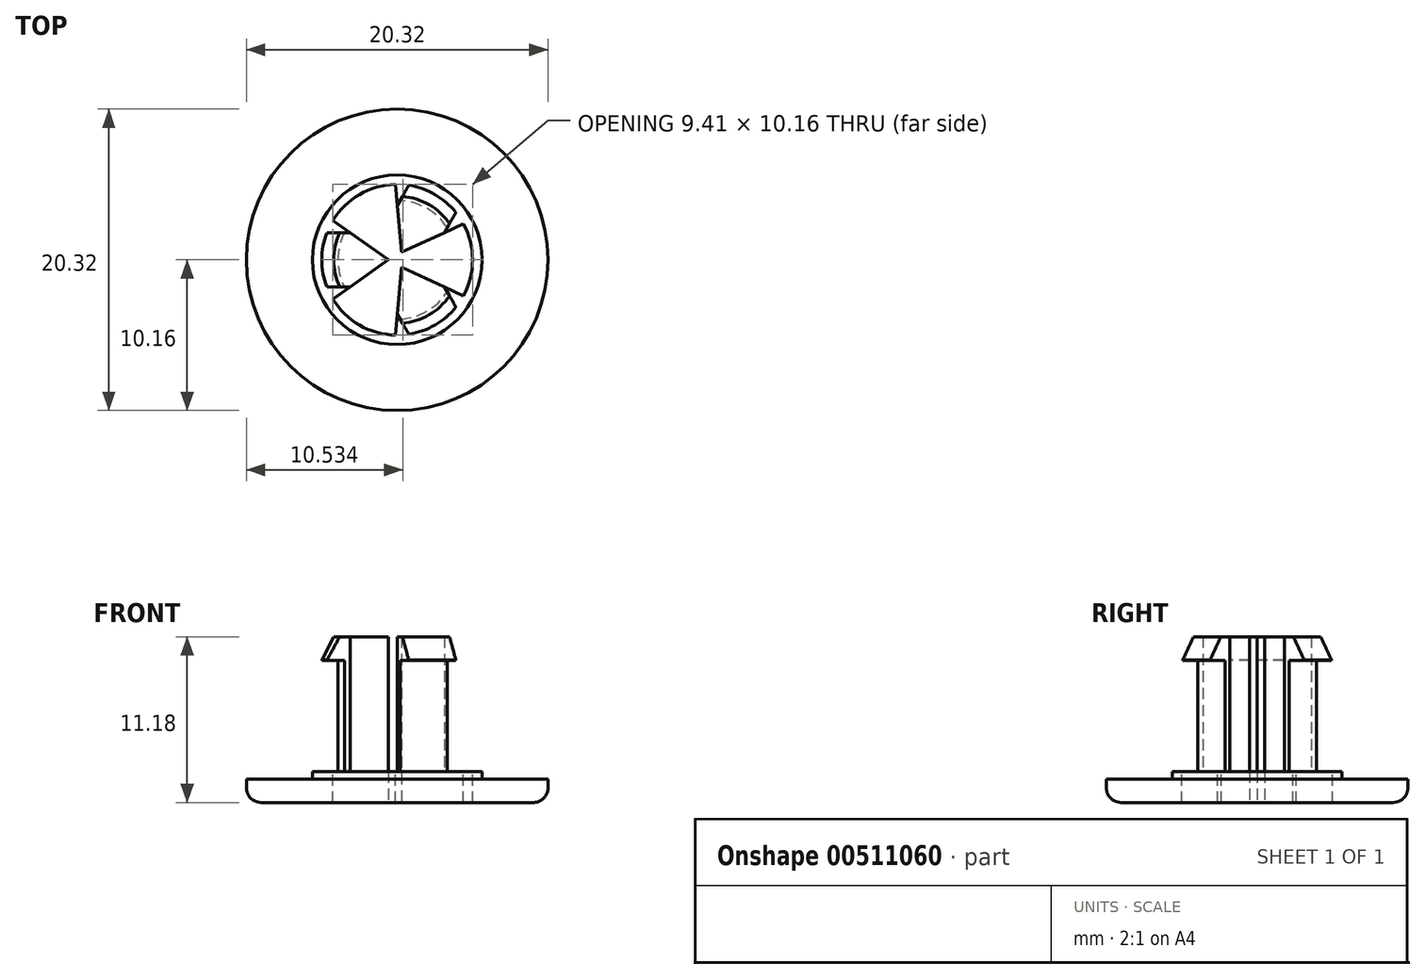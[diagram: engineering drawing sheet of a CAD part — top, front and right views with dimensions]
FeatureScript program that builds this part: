
annotation { "Feature Type Name" : "Feature", "Feature Type Description" : "" }
export const myFeature = defineFeature(function(context is Context, id is Id, definition is map)
    precondition{}
    {
        {
            var Q0;
            Q0=qCreatedBy(makeId("Top.planeOp"),FACE);
            var sketch = newSketch(context, id + "F0", { "sketchPlane" : qUnion([Q0])});
            skCircle(sketch, "E0", {"center": v(0, 0) * mm, "radius": 10.16 * mm});
            skSolve(sketch);
        }
        {
            var Q0;
            Q0=makeQuery(id+"F0.imprint","IMPRINT",FACE,{"disambiguationData":[TD([[makeQuery(id+"F0.imprint","IMPRINT",EDGE,{"derivedFrom":sQuery(id+"F0.wireOp",EDGE,"E0")}),1.0]])]});
            extrude(context, id + "F1", {"entities" : qUnion([Q0]), "depth" : 1.59 * mm});
        }
        {
            var Q0;
            Q0=makeQuery(id+"F1.opExtrude","CAP_FACE",FACE,{"disambiguationData":[OSD([sQuery(id+"F0.wireOp",EDGE,"E0")])],"isStart":false});
            var sketch = newSketch(context, id + "F2", { "sketchPlane" : qUnion([Q0])});
            skCircle(sketch, "E1", {"center": v(0, 0) * mm, "radius": 4 * mm});
            skCircle(sketch, "E2.cCircle", {"center": v(0, 0) * mm, "radius": 3.18 * mm, "construction": true});
            skLineSegment(sketch, "E2.0", {"start": v(3.18, 1.83) * mm, "end": v(3.18, -1.83) * mm});
            skLineSegment(sketch, "E2.1", {"start": v(3.17, -1.83) * mm, "end": v(0, -3.67) * mm});
            skLineSegment(sketch, "E2.2", {"start": v(0, -3.67) * mm, "end": v(-3.18, -1.83) * mm});
            skLineSegment(sketch, "E2.3", {"start": v(-3.18, -1.83) * mm, "end": v(-3.18, 1.83) * mm});
            skLineSegment(sketch, "E2.4", {"start": v(-3.18, 1.83) * mm, "end": v(0, 3.67) * mm});
            skLineSegment(sketch, "E2.5", {"start": v(0, 3.67) * mm, "end": v(3.18, 1.83) * mm});
            skPoint(sketch, "E2.0.midPoint", {"position": v(3.18, 0) * mm});
            skLineSegment(sketch, "E3", {"start": v(0, 3.67) * mm, "end": v(0.3, 0.5) * mm});
            skLineSegment(sketch, "E4", {"start": v(0.3, 0.5) * mm, "end": v(3.17, 1.83) * mm});
            skLineSegment(sketch, "E5", {"start": v(0.3, -0.5) * mm, "end": v(0, -3.67) * mm});
            skLineSegment(sketch, "E6", {"start": v(-0.58, 0) * mm, "end": v(-3.18, -1.83) * mm});
            skLineSegment(sketch, "E7", {"start": v(-3.18, 1.83) * mm, "end": v(-0.58, 0) * mm});
            skLineSegment(sketch, "E8", {"start": v(0.3, -0.5) * mm, "end": v(3.18, -1.83) * mm});
            skSolve(sketch);
        }
        {
            var Q0;
            Q0=makeQuery(id+"F2.imprint","IMPRINT",FACE,{"disambiguationData":[TD([[makeQuery(id+"F2.imprint","IMPRINT",EDGE,{"derivedFrom":sQuery(id+"F2.wireOp",EDGE,"E1")}),1.0]])]});
            var Q1;
            Q1=makeQuery(id+"F2.imprint","IMPRINT",FACE,{"disambiguationData":[TD([[makeQuery(id+"F2.imprint","IMPRINT",EDGE,{"derivedFrom":sQuery(id+"F2.wireOp",EDGE,"E2.3")}),-1.0]])]});
            var Q2;
            Q2=makeQuery(id+"F2.imprint","IMPRINT",FACE,{"disambiguationData":[TD([[makeQuery(id+"F2.imprint","IMPRINT",EDGE,{"derivedFrom":sQuery(id+"F2.wireOp",EDGE,"E2.5")}),-1.0]])]});
            var Q3;
            Q3=makeQuery(id+"F2.imprint","IMPRINT",FACE,{"disambiguationData":[TD([[makeQuery(id+"F2.imprint","IMPRINT",EDGE,{"derivedFrom":sQuery(id+"F2.wireOp",EDGE,"E2.1")}),-1.0]])]});
            extrude(context, id + "F3", {"entities" : qUnion([Q0, Q1, Q2, Q3]), "operationType" : NewBodyOperationType.ADD, "depth" : 8 * mm, "offsetDistance" : 25.4 * mm});
        }
        {
            var Q0;
            Q0=makeQuery(id+"F3.opExtrude","CAP_FACE",FACE,{"disambiguationData":[OSD([sQuery(id+"F2.wireOp",EDGE,"E1"),sQuery(id+"F2.wireOp",EDGE,"E2.0"),sQuery(id+"F2.wireOp",EDGE,"E2.2"),sQuery(id+"F2.wireOp",EDGE,"E2.4"),sQuery(id+"F2.wireOp",EDGE,"E3"),sQuery(id+"F2.wireOp",EDGE,"E4"),sQuery(id+"F2.wireOp",EDGE,"E5"),sQuery(id+"F2.wireOp",EDGE,"E6"),sQuery(id+"F2.wireOp",EDGE,"E7"),sQuery(id+"F2.wireOp",EDGE,"E8")])],"isStart":false});
            var sketch = newSketch(context, id + "F4", { "sketchPlane" : qUnion([Q0])});
            skLineSegment(sketch, "E9", {"start": v(0, 3.67) * mm, "end": v(3.18, 1.83) * mm});
            skLineSegment(sketch, "E10", {"start": v(3.17, 1.83) * mm, "end": v(3.37, 2.16) * mm});
            skLineSegment(sketch, "E11", {"start": v(0, 3.67) * mm, "end": v(0.2, 4) * mm});
            skLineSegment(sketch, "E12", {"start": v(-3.18, 1.83) * mm, "end": v(-3.18, -1.83) * mm});
            skLineSegment(sketch, "E13", {"start": v(-3.18, -1.83) * mm, "end": v(-3.56, -1.83) * mm});
            skLineSegment(sketch, "E14", {"start": v(-3.18, 1.83) * mm, "end": v(-3.56, 1.83) * mm});
            skLineSegment(sketch, "E15", {"start": v(0, -3.67) * mm, "end": v(3.18, -1.83) * mm});
            skLineSegment(sketch, "E16", {"start": v(3.18, -1.83) * mm, "end": v(3.37, -2.16) * mm});
            skLineSegment(sketch, "E17", {"start": v(0, -3.67) * mm, "end": v(0.2, -4) * mm});
            skSolve(sketch);
        }
        {
            var Q0;
            {var subQ0=sQuery(id+"F4.wireOp",EDGE,"E11");Q0=makeQuery(id+"F4.imprint","IMPRINT",FACE,{"disambiguationData":[TD([[makeQuery(id+"F4.imprint","IMPRINT",EDGE,{"derivedFrom":subQ0}),1.0]])]});}
            var Q1;
            {var subQ0=sQuery(id+"F4.wireOp",EDGE,"E10");Q1=makeQuery(id+"F4.imprint","IMPRINT",FACE,{"disambiguationData":[TD([[makeQuery(id+"F4.imprint","IMPRINT",EDGE,{"derivedFrom":subQ0}),-1.0]])]});}
            var Q2;
            {var subQ0=sQuery(id+"F4.wireOp",EDGE,"E13");Q2=makeQuery(id+"F4.imprint","IMPRINT",FACE,{"disambiguationData":[TD([[makeQuery(id+"F4.imprint","IMPRINT",EDGE,{"derivedFrom":subQ0}),1.0]])]});}
            var Q3;
            {var subQ0=sQuery(id+"F0.wireOp",EDGE,"E0");Q3=makeQuery(id+"F3.boolean.opBoolean","SPLIT",FACE,{"disambiguationData":[TD([makeQuery(id+"F1.opExtrude","SWEPT_FACE",FACE,{"disambiguationData":[OSD([subQ0])]})])],"derivedFrom":makeQuery(id+"F1.opExtrude","CAP_FACE",FACE,{"disambiguationData":[OSD([subQ0])],"isStart":false})});}
            extrude(context, id + "F5", {"entities" : qUnion([Q0, Q1, Q2]), "operationType" : NewBodyOperationType.REMOVE, "endBound" : BoundingType.UP_TO_SURFACE, "oppositeDirection" : true, "depth" : 25.4 * mm, "endBoundEntityFace" : qUnion([Q3]), "offsetDistance" : 25.4 * mm});
        }
        {
            var Q0;
            {var subQ0=sQuery(id+"F2.wireOp",EDGE,"E2.2");var subQ1=sQuery(id+"F2.wireOp",EDGE,"E1");var subQ2=sQuery(id+"F2.wireOp",EDGE,"E2.4");var subQ3=sQuery(id+"F2.wireOp",EDGE,"E2.0");var subQ4=sQuery(id+"F0.wireOp",EDGE,"E0");var subQ5=makeQuery(id+"F1.opExtrude","CAP_FACE",FACE,{"disambiguationData":[OSD([subQ4])],"isStart":false});Q0=makeQuery(id+"F5.boolean.opBoolean","MERGE",FACE,{"derivedFrom":[makeQuery(id+"F3.boolean.opBoolean","SPLIT",FACE,{"disambiguationData":[TD([makeQuery(id+"F1.opExtrude","SWEPT_FACE",FACE,{"disambiguationData":[OSD([subQ4])]})])],"derivedFrom":subQ5}),makeQuery(id+"F3.boolean.opBoolean","SPLIT",FACE,{"disambiguationData":[TD([makeQuery(id+"F3.opExtrude","SWEPT_FACE",FACE,{"disambiguationData":[OSD([subQ3])]})])],"derivedFrom":subQ5}),makeQuery(id+"F5.opExtrude","CAP_FACE",FACE,{"disambiguationData":[OSD([subQ1,subQ3,sQuery(id+"F4.wireOp",EDGE,"E10"),sQuery(id+"F4.wireOp",EDGE,"E16")])],"isStart":false}),makeQuery(id+"F5.opExtrude","CAP_FACE",FACE,{"disambiguationData":[OSD([subQ1,subQ2,sQuery(id+"F4.wireOp",EDGE,"E11"),sQuery(id+"F4.wireOp",EDGE,"E14")])],"isStart":false}),makeQuery(id+"F5.opExtrude","CAP_FACE",FACE,{"disambiguationData":[OSD([subQ1,subQ0,sQuery(id+"F4.wireOp",EDGE,"E13"),sQuery(id+"F4.wireOp",EDGE,"E17")])],"isStart":false})]});}
            var sketch = newSketch(context, id + "F6", { "sketchPlane" : qUnion([Q0])});
            skCircle(sketch, "E18", {"center": v(0, 0) * mm, "radius": 5.71 * mm});
            skSolve(sketch);
        }
        {
            var Q0;
            Q0 = qSketchRegion(id + "F6", true);
            extrude(context, id + "F7", {"entities" : qUnion([Q0]), "operationType" : NewBodyOperationType.ADD, "depth" : .5 * mm, "offsetDistance" : 25.4 * mm});
        }
        {
            var Q0;
            {var subQ0=sQuery(id+"F2.wireOp",EDGE,"E4");var subQ1=sQuery(id+"F2.wireOp",EDGE,"E3");var subQ2=sQuery(id+"F2.wireOp",EDGE,"E1");Q0=makeQuery(id+"F5.boolean.opBoolean","SPLIT",FACE,{"disambiguationData":[TD([makeQuery(id+"F3.opExtrude","SWEPT_FACE",FACE,{"disambiguationData":[OSD([subQ1])]})])],"derivedFrom":makeQuery(id+"F3.opExtrude","CAP_FACE",FACE,{"disambiguationData":[OSD([subQ2,sQuery(id+"F2.wireOp",EDGE,"E2.0"),sQuery(id+"F2.wireOp",EDGE,"E2.2"),sQuery(id+"F2.wireOp",EDGE,"E2.4"),subQ1,subQ0,sQuery(id+"F2.wireOp",EDGE,"E5"),sQuery(id+"F2.wireOp",EDGE,"E6"),sQuery(id+"F2.wireOp",EDGE,"E7"),sQuery(id+"F2.wireOp",EDGE,"E8")])],"isStart":false})});}
            var sketch = newSketch(context, id + "F8", { "sketchPlane" : qUnion([Q0])});
            skLineSegment(sketch, "E19.0", {"start": v(0, 3.67) * mm, "end": v(0.3, 0.5) * mm});
            skLineSegment(sketch, "E20.0", {"start": v(0, 3.67) * mm, "end": v(0.2, 4) * mm});
            skArc(sketch, "E21.0", {"start": v(3.37, 2.16) * mm, "mid": v(2, 3.46) * mm, "end": v(0.2, 4) * mm});
            skLineSegment(sketch, "E22.0", {"start": v(3.18, 1.83) * mm, "end": v(3.37, 2.16) * mm});
            skLineSegment(sketch, "E23.0", {"start": v(0.3, 0.5) * mm, "end": v(3.18, 1.83) * mm});
            skLineSegment(sketch, "E24.0", {"start": v(0.3, -0.5) * mm, "end": v(3.17, -1.83) * mm});
            skLineSegment(sketch, "E25.0", {"start": v(0.3, -0.5) * mm, "end": v(0, -3.67) * mm});
            skLineSegment(sketch, "E26.0", {"start": v(3.18, -1.83) * mm, "end": v(3.37, -2.16) * mm});
            skArc(sketch, "E27.0", {"start": v(0.2, -4) * mm, "mid": v(2, -3.46) * mm, "end": v(3.37, -2.16) * mm});
            skLineSegment(sketch, "E28.0", {"start": v(0, -3.67) * mm, "end": v(0.2, -4) * mm});
            skPoint(sketch, "E29.0", {"position": v(-1.88, -0.92) * mm});
            skLineSegment(sketch, "E30.0", {"start": v(-0.58, 0) * mm, "end": v(-3.18, -1.83) * mm});
            skLineSegment(sketch, "E31.0", {"start": v(-3.18, 1.83) * mm, "end": v(-0.58, 0) * mm});
            skPoint(sketch, "E32.0", {"position": v(-3.56, 1.83) * mm});
            skLineSegment(sketch, "E33.0", {"start": v(-3.18, 1.83) * mm, "end": v(-3.56, 1.83) * mm});
            skArc(sketch, "E34.0", {"start": v(-3.56, 1.83) * mm, "mid": v(-4, 0) * mm, "end": v(-3.56, -1.83) * mm});
            skLineSegment(sketch, "E35.0.0", {"start": v(-3.56, -1.83) * mm, "end": v(-3.18, -1.83) * mm});
            skLineSegment(sketch, "E35.0.1", {"start": v(-3.18, -1.83) * mm, "end": v(-0.58, 0) * mm});
            skLineSegment(sketch, "E35.0.2", {"start": v(-0.58, 0) * mm, "end": v(-3.18, 1.83) * mm});
            skArc(sketch, "E36", {"start": v(-4.74, 1.83) * mm, "mid": v(-5.08, 0) * mm, "end": v(-4.74, -1.83) * mm});
            skLineSegment(sketch, "E37", {"start": v(0.2, 4) * mm, "end": v(3.37, 2.16) * mm});
            skLineSegment(sketch, "E38", {"start": v(3.37, 2.16) * mm, "end": v(3.96, 3.19) * mm});
            skLineSegment(sketch, "E39", {"start": v(0.2, 4) * mm, "end": v(0.78, 5.02) * mm});
            skLineSegment(sketch, "E40", {"start": v(-3.56, 1.83) * mm, "end": v(-3.56, -1.83) * mm});
            skLineSegment(sketch, "E41", {"start": v(-3.56, -1.83) * mm, "end": v(-4.74, -1.83) * mm});
            skLineSegment(sketch, "E42", {"start": v(-3.56, 1.83) * mm, "end": v(-4.74, 1.83) * mm});
            skLineSegment(sketch, "E43", {"start": v(0.2, -4) * mm, "end": v(3.37, -2.16) * mm});
            skLineSegment(sketch, "E44", {"start": v(3.37, -2.16) * mm, "end": v(3.96, -3.19) * mm});
            skLineSegment(sketch, "E45", {"start": v(0.2, -4) * mm, "end": v(0.78, -5.02) * mm});
            skArc(sketch, "E46.trimOffspring", {"start": v(3.96, 3.19) * mm, "mid": v(2.54, 4.4) * mm, "end": v(0.78, 5.02) * mm});
            skArc(sketch, "E47.trimOffspring", {"start": v(0.78, -5.02) * mm, "mid": v(2.54, -4.4) * mm, "end": v(3.96, -3.19) * mm});
            skSolve(sketch);
        }
        {
            var Q0;
            Q0=makeQuery(id+"F8.imprint","IMPRINT",FACE,{"disambiguationData":[TD([[makeQuery(id+"F8.imprint","IMPRINT",EDGE,{"derivedFrom":sQuery(id+"F8.wireOp",EDGE,"E35.0.0")}),1.0]])]});
            var Q1;
            Q1=makeQuery(id+"F8.imprint","IMPRINT",FACE,{"disambiguationData":[TD([[makeQuery(id+"F8.imprint","IMPRINT",EDGE,{"derivedFrom":sQuery(id+"F8.wireOp",EDGE,"E34.0")}),1.0]])]});
            var Q2;
            Q2=makeQuery(id+"F8.imprint","IMPRINT",FACE,{"disambiguationData":[TD([[makeQuery(id+"F8.imprint","IMPRINT",EDGE,{"derivedFrom":sQuery(id+"F8.wireOp",EDGE,"E34.0")}),-1.0]])]});
            var Q3;
            Q3=makeQuery(id+"F8.imprint","IMPRINT",FACE,{"disambiguationData":[TD([[makeQuery(id+"F8.imprint","IMPRINT",EDGE,{"derivedFrom":sQuery(id+"F8.wireOp",EDGE,"E19.0")}),1.0]])]});
            var Q4;
            Q4=makeQuery(id+"F8.imprint","IMPRINT",FACE,{"disambiguationData":[TD([[makeQuery(id+"F8.imprint","IMPRINT",EDGE,{"derivedFrom":sQuery(id+"F8.wireOp",EDGE,"E21.0")}),1.0]])]});
            var Q5;
            Q5=makeQuery(id+"F8.imprint","IMPRINT",FACE,{"disambiguationData":[TD([[makeQuery(id+"F8.imprint","IMPRINT",EDGE,{"derivedFrom":sQuery(id+"F8.wireOp",EDGE,"E21.0")}),-1.0]])]});
            var Q6;
            Q6=makeQuery(id+"F8.imprint","IMPRINT",FACE,{"disambiguationData":[TD([[makeQuery(id+"F8.imprint","IMPRINT",EDGE,{"derivedFrom":sQuery(id+"F8.wireOp",EDGE,"E24.0")}),-1.0]])]});
            var Q7;
            Q7=makeQuery(id+"F8.imprint","IMPRINT",FACE,{"disambiguationData":[TD([[makeQuery(id+"F8.imprint","IMPRINT",EDGE,{"derivedFrom":sQuery(id+"F8.wireOp",EDGE,"E27.0")}),1.0]])]});
            var Q8;
            Q8=makeQuery(id+"F8.imprint","IMPRINT",FACE,{"disambiguationData":[TD([[makeQuery(id+"F8.imprint","IMPRINT",EDGE,{"derivedFrom":sQuery(id+"F8.wireOp",EDGE,"E27.0")}),-1.0]])]});
            extrude(context, id + "F9", {"entities" : qUnion([Q0, Q1, Q2, Q3, Q4, Q5, Q6, Q7, Q8]), "operationType" : NewBodyOperationType.ADD, "depth" : 1.59 * mm, "offsetDistance" : 25.4 * mm});
        }
        {
            var Q0;
            Q0=makeQuery(id+"F9.opExtrude","CAP_EDGE",EDGE,{"disambiguationData":[OSD([sQuery(id+"F8.wireOp",EDGE,"E47.trimOffspring")])],"isStart":false});
            var Q1;
            Q1=makeQuery(id+"F9.opExtrude","CAP_EDGE",EDGE,{"disambiguationData":[OSD([sQuery(id+"F8.wireOp",EDGE,"E46.trimOffspring")])],"isStart":false});
            var Q2;
            Q2=makeQuery(id+"F9.opExtrude","CAP_EDGE",EDGE,{"disambiguationData":[OSD([sQuery(id+"F8.wireOp",EDGE,"E36")])],"isStart":false});
            chamfer(context, id + "F10", {"entities" : qUnion([Q0, Q1, Q2]), "chamferType" : ChamferType.TWO_OFFSETS, "width1" : 0.8 * mm, "oppositeDirection" : false, "width2" : 1.57 * mm, "tangentPropagation" : true});
        }
        {
            var Q0;
            Q0=makeQuery(id+"F7.opExtrude","CAP_FACE",FACE,{"disambiguationData":[OSD([sQuery(id+"F6.wireOp",EDGE,"E18")])],"isStart":false});
            var sketch = newSketch(context, id + "F11", { "sketchPlane" : qUnion([Q0])});
            skCircle(sketch, "E48", {"center": v(0, 0) * mm, "radius": 5.08 * mm});
            skCircle(sketch, "E49.0.0", {"center": v(0, 0) * mm, "radius": 5.71 * mm});
            skLineSegment(sketch, "E50.0", {"start": v(0, 3.67) * mm, "end": v(0.3, 0.5) * mm});
            skLineSegment(sketch, "E50.1", {"start": v(-0.58, 0) * mm, "end": v(-3.18, 1.83) * mm});
            skLineSegment(sketch, "E51.0", {"start": v(-3.18, -1.83) * mm, "end": v(-0.58, 0) * mm});
            skLineSegment(sketch, "E51.1", {"start": v(0.3, -0.5) * mm, "end": v(0, -3.67) * mm});
            skLineSegment(sketch, "E51.2", {"start": v(0.3, -0.5) * mm, "end": v(3.17, -1.83) * mm});
            skLineSegment(sketch, "E51.3", {"start": v(0.3, 0.5) * mm, "end": v(3.18, 1.83) * mm});
            skLineSegment(sketch, "E52", {"start": v(3.18, 1.83) * mm, "end": v(4.46, 2.43) * mm});
            skLineSegment(sketch, "E53", {"start": v(0, 3.67) * mm, "end": v(-0.13, 5.08) * mm});
            skLineSegment(sketch, "E54", {"start": v(-3.18, 1.83) * mm, "end": v(-4.33, 2.65) * mm});
            skLineSegment(sketch, "E55", {"start": v(-3.18, -1.83) * mm, "end": v(-4.33, -2.65) * mm});
            skLineSegment(sketch, "E56", {"start": v(0, -3.67) * mm, "end": v(-0.13, -5.08) * mm});
            skLineSegment(sketch, "E57", {"start": v(3.17, -1.83) * mm, "end": v(4.46, -2.43) * mm});
            skSolve(sketch);
        }
        {
            var Q0;
            Q0=makeQuery(id+"F11.imprint","IMPRINT",FACE,{"disambiguationData":[TD([[makeQuery(id+"F11.imprint","IMPRINT",EDGE,{"derivedFrom":sQuery(id+"F11.wireOp",EDGE,"E50.0")}),-1.0]])]});
            extrude(context, id + "F12", {"entities" : qUnion([Q0]), "operationType" : NewBodyOperationType.REMOVE, "endBound" : BoundingType.THROUGH_ALL, "oppositeDirection" : true, "depth" : 25.4 * mm, "offsetDistance" : 25.4 * mm});
        }
        {
            var Q0;
            Q0=makeQuery(id+"F1.opExtrude","CAP_EDGE",EDGE,{"disambiguationData":[OSD([sQuery(id+"F0.wireOp",EDGE,"E0")])],"isStart":true});
            fillet(context, id + "F13", {"entities" : qUnion([Q0]), "radius" : 1 * mm, "tangentPropagation" : true, "allowEdgeOverflow" : false});
        }
    });
